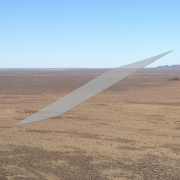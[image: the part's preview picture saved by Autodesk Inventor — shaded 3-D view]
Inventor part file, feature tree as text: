
AUTODESK INVENTOR PART (.ipt)
format: ipt  version: 2014 SP1 (Build 180222100, 222)  size: 152,576 bytes
history: native  units: in
note: dims shown in document units (in); Inventor stores cm internally (conversion verified against a paired STEP export)
features: sketch x3, sweep x1, extrude x1, other x1
ambient origin geometry x8: Origin, YZ Plane, XZ Plane, XY Plane, X Axis, Y Axis, Z Axis, Center Point
bodies: Body1 (feature_tree)
feature tree (6):
  sweep  "Sweep2"
  extrude  "Extrusion3"  TaperAngle=0.0deg  [1 undecoded]
  sketch  "Sketch3"  dims[d6=0.0in d7=275.0in d8=90.0in]
  other  "2D Equation Curve2"
  sketch  "Sketch4"  dims[d10=0.25in d11=0.0in]
  sketch  "Sketch8"  dims[d28=2.0in d29=2.0in d32=2.0in d33=300.0in d34=1.1853in d35=238.0in d36=277.0in d37=300.0in d38=0.0in]
note: 1 required parameter value undecoded (feature->parameter linkage not recoverable at this tier; creation-order binding heuristic only, values carry confidence <= 0.55)
